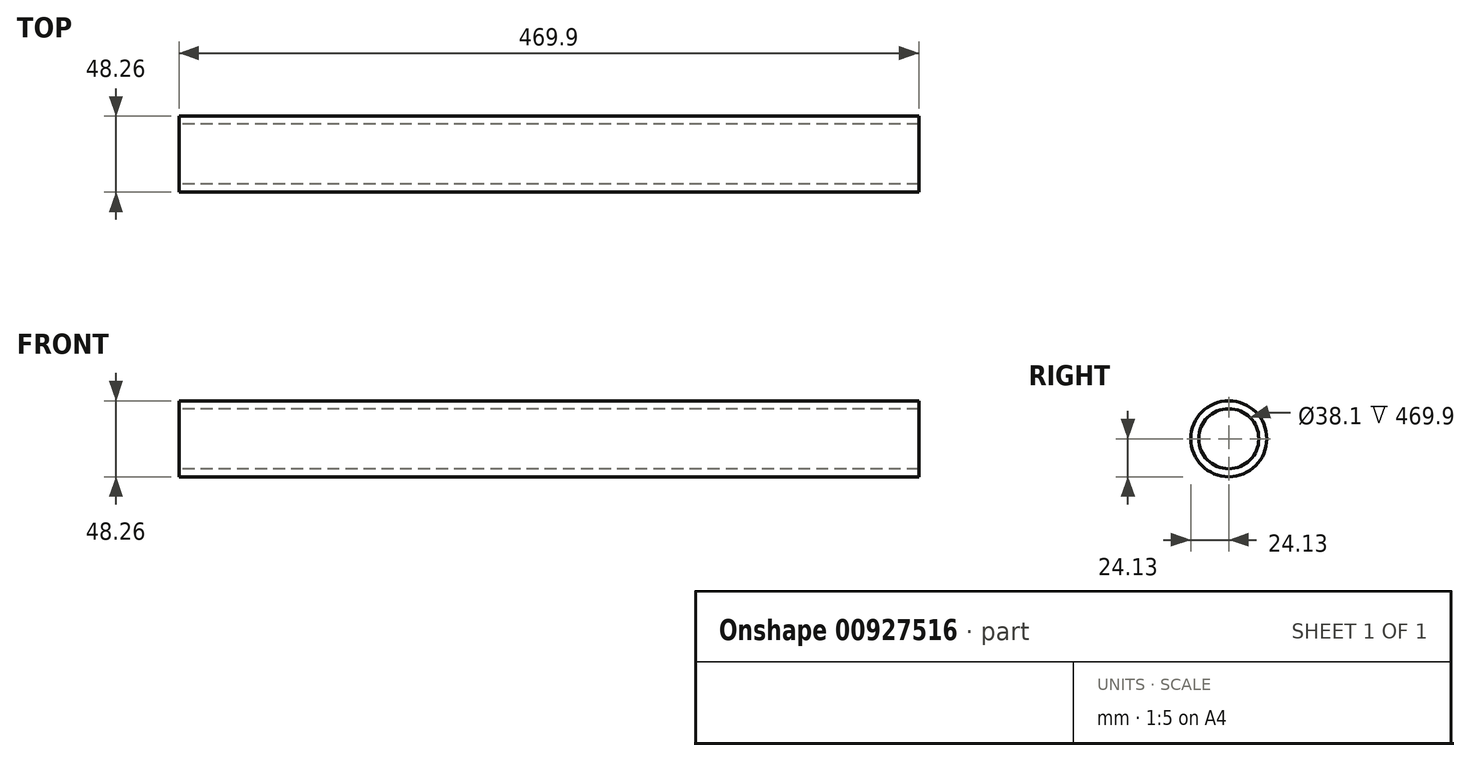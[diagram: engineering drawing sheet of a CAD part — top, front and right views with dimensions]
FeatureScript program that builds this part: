
annotation { "Feature Type Name" : "Feature", "Feature Type Description" : "" }
export const myFeature = defineFeature(function(context is Context, id is Id, definition is map)
    precondition{}
    {
        {
            var Q0;
            Q0=qCreatedBy(makeId("Right.planeOp"),FACE);
            var sketch = newSketch(context, id + "F0", { "sketchPlane" : qUnion([Q0])});
            skCircle(sketch, "E0", {"center": v(0, 0) * mm, "radius": 24.13 * mm});
            skCircle(sketch, "E1", {"center": v(0, 0) * mm, "radius": 19.05 * mm});
            skSolve(sketch);
        }
        {
            var Q0;
            Q0=makeQuery(id+"F0.imprint","IMPRINT",FACE,{"disambiguationData":[TD([[makeQuery(id+"F0.imprint","IMPRINT",EDGE,{"derivedFrom":sQuery(id+"F0.wireOp",EDGE,"E0")}),1.0]])]});
            extrude(context, id + "F1", {"entities" : qUnion([Q0]), "depth" : 469.9 * mm, "offsetDistance" : 25.4 * mm});
        }
    });
